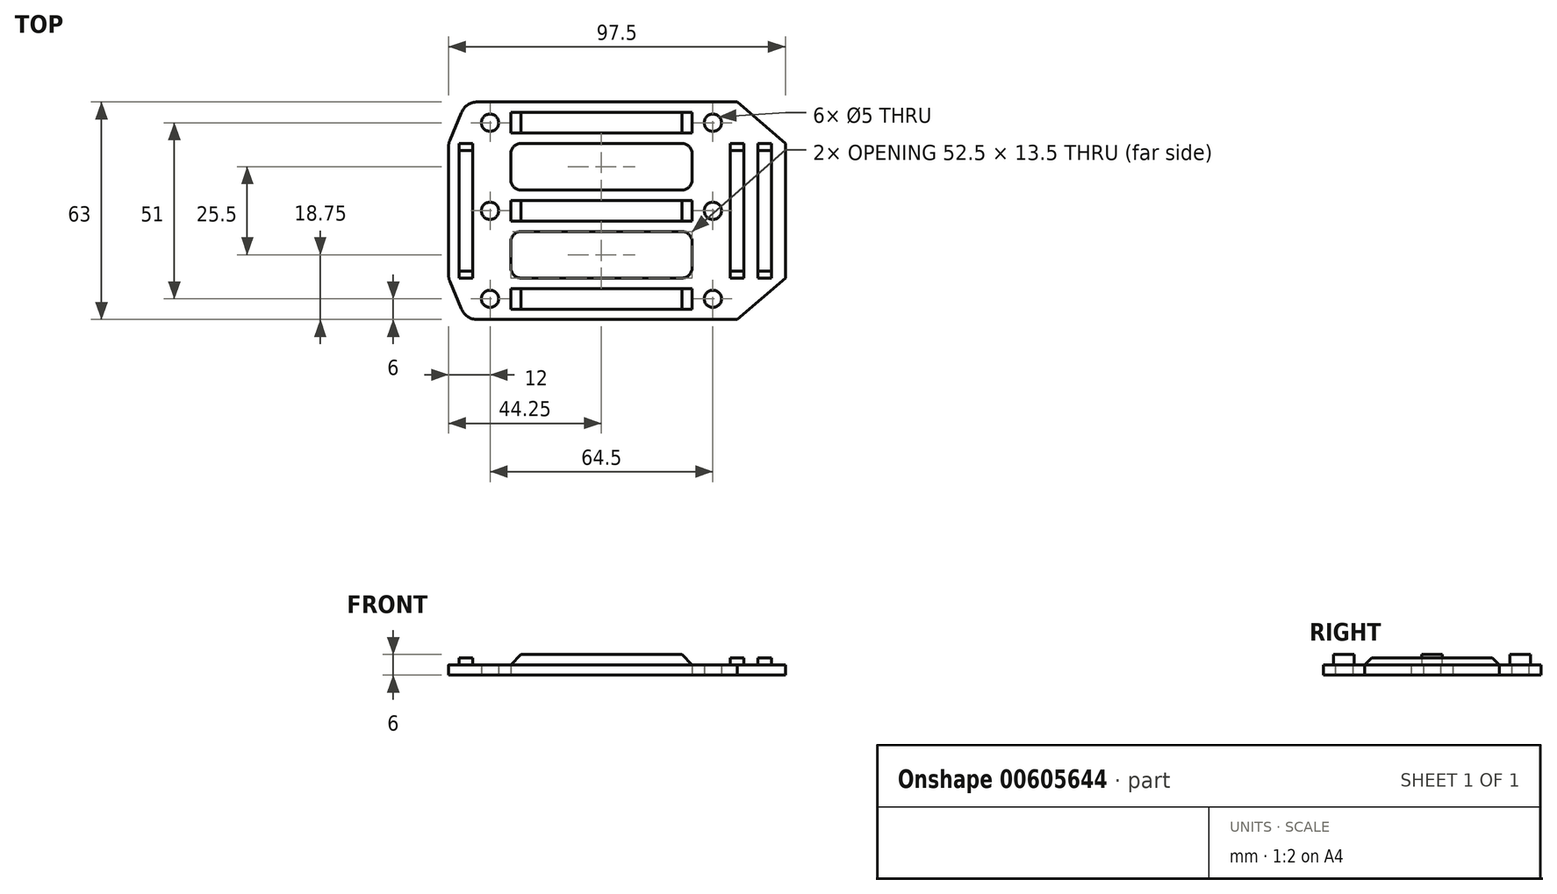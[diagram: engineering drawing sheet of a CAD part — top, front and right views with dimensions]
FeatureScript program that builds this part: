
annotation { "Feature Type Name" : "Feature", "Feature Type Description" : "" }
export const myFeature = defineFeature(function(context is Context, id is Id, definition is map)
    precondition{}
    {
        {
            var Q0;
            Q0=qCreatedBy(makeId("Top.planeOp"),FACE);
            var sketch = newSketch(context, id + "F0", { "sketchPlane" : qUnion([Q0])});
            skLineSegment(sketch, "E0.bottom", {"start": v(32.25, -25.5) * mm, "end": v(-32.25, -25.5) * mm});
            skLineSegment(sketch, "E0.top", {"start": v(32.25, 25.5) * mm, "end": v(-32.25, 25.5) * mm});
            skLineSegment(sketch, "E0.left", {"start": v(32.25, -25.5) * mm, "end": v(32.25, 25.5) * mm});
            skLineSegment(sketch, "E0.right", {"start": v(-32.25, -25.5) * mm, "end": v(-32.25, 25.5) * mm});
            skPoint(sketch, "E0.middle", {"position": v(0, 0) * mm});
            skLineSegment(sketch, "E1.0", {"start": v(-38.25, -28.5) * mm, "end": v(-38.25, 28.5) * mm});
            skLineSegment(sketch, "E1.1", {"start": v(35.25, -31.5) * mm, "end": v(-35.25, -31.5) * mm});
            skLineSegment(sketch, "E1.2", {"start": v(38.25, -28.5) * mm, "end": v(38.25, 28.5) * mm});
            skLineSegment(sketch, "E1.3", {"start": v(35.25, 31.5) * mm, "end": v(-35.25, 31.5) * mm});
            skCircle(sketch, "E2", {"center": v(-32.25, 25.5) * mm, "radius": 2.5 * mm});
            skCircle(sketch, "E3", {"center": v(-32.25, -25.5) * mm, "radius": 2.5 * mm});
            skCircle(sketch, "E4", {"center": v(32.25, 25.5) * mm, "radius": 2.5 * mm});
            skCircle(sketch, "E5", {"center": v(32.25, -25.5) * mm, "radius": 2.5 * mm});
            skCircle(sketch, "E6", {"center": v(-32.25, 0) * mm, "radius": 2.5 * mm});
            skCircle(sketch, "E7", {"center": v(32.25, 0) * mm, "radius": 2.5 * mm});
            skLineSegment(sketch, "E8.0", {"start": v(-26.25, -16.5) * mm, "end": v(-26.25, -9) * mm});
            skLineSegment(sketch, "E8.1", {"start": v(23.25, -19.5) * mm, "end": v(-23.25, -19.5) * mm});
            skLineSegment(sketch, "E8.2", {"start": v(26.25, -16.5) * mm, "end": v(26.25, -9) * mm});
            skLineSegment(sketch, "E8.3", {"start": v(23.25, 19.5) * mm, "end": v(-23.25, 19.5) * mm});
            skLineSegment(sketch, "E9", {"start": v(-32.25, 0) * mm, "end": v(32.25, 0) * mm, "construction": true});
            skLineSegment(sketch, "E10.0", {"start": v(-23.25, -6) * mm, "end": v(23.25, -6) * mm});
            skLineSegment(sketch, "E11.0", {"start": v(-23.25, 6) * mm, "end": v(23.25, 6) * mm});
            skPoint(sketch, "E12.visualSharp", {"position": v(-26.25, -19.5) * mm});
            skArc(sketch, "E12.filletArc", {"start": v(-26.25, -16.5) * mm, "mid": v(-25.37, -18.62) * mm, "end": v(-23.25, -19.5) * mm});
            skPoint(sketch, "E13.visualSharp", {"position": v(26.25, -19.5) * mm});
            skArc(sketch, "E13.filletArc", {"start": v(23.25, -19.5) * mm, "mid": v(25.37, -18.62) * mm, "end": v(26.25, -16.5) * mm});
            skPoint(sketch, "E14.visualSharp", {"position": v(26.25, 19.5) * mm});
            skArc(sketch, "E14.filletArc", {"start": v(26.25, 16.5) * mm, "mid": v(25.37, 18.62) * mm, "end": v(23.25, 19.5) * mm});
            skPoint(sketch, "E15.visualSharp", {"position": v(-26.25, 19.5) * mm});
            skArc(sketch, "E15.filletArc", {"start": v(-23.25, 19.5) * mm, "mid": v(-25.37, 18.62) * mm, "end": v(-26.25, 16.5) * mm});
            skPoint(sketch, "E16", {"position": v(-26.25, -6) * mm});
            skPoint(sketch, "E17", {"position": v(-26.25, 6) * mm});
            skLineSegment(sketch, "E18.trimOffspring", {"start": v(-26.25, 9) * mm, "end": v(-26.25, 16.5) * mm});
            skLineSegment(sketch, "E19.trimOffspring", {"start": v(26.25, 9) * mm, "end": v(26.25, 16.5) * mm});
            skArc(sketch, "E20.filletArc", {"start": v(-26.25, 9) * mm, "mid": v(-25.37, 6.88) * mm, "end": v(-23.25, 6) * mm});
            skArc(sketch, "E21.filletArc", {"start": v(23.25, 6) * mm, "mid": v(25.37, 6.88) * mm, "end": v(26.25, 9) * mm});
            skArc(sketch, "E22.filletArc", {"start": v(-23.25, -6) * mm, "mid": v(-25.37, -6.88) * mm, "end": v(-26.25, -9) * mm});
            skArc(sketch, "E23.filletArc", {"start": v(26.25, -9) * mm, "mid": v(25.37, -6.88) * mm, "end": v(23.25, -6) * mm});
            skPoint(sketch, "E24.visualSharp", {"position": v(-38.25, 31.5) * mm});
            skPoint(sketch, "E25.visualSharp", {"position": v(38.25, 31.5) * mm});
            skPoint(sketch, "E26.visualSharp", {"position": v(38.25, -31.5) * mm});
            skPoint(sketch, "E27.visualSharp", {"position": v(-38.25, -31.5) * mm});
            skLineSegment(sketch, "E28.bottom", {"start": v(26.25, -22.5) * mm, "end": v(-26.25, -22.5) * mm});
            skLineSegment(sketch, "E28.top", {"start": v(26.25, -28.5) * mm, "end": v(-26.25, -28.5) * mm});
            skLineSegment(sketch, "E28.left", {"start": v(26.25, -22.5) * mm, "end": v(26.25, -28.5) * mm});
            skLineSegment(sketch, "E28.right", {"start": v(-26.25, -22.5) * mm, "end": v(-26.25, -28.5) * mm});
            skPoint(sketch, "E28.middle", {"position": v(0, -25.5) * mm});
            skLineSegment(sketch, "E29.bottom", {"start": v(26.25, 22.5) * mm, "end": v(-26.25, 22.5) * mm});
            skLineSegment(sketch, "E29.top", {"start": v(26.25, 28.5) * mm, "end": v(-26.25, 28.5) * mm});
            skLineSegment(sketch, "E29.left", {"start": v(26.25, 22.5) * mm, "end": v(26.25, 28.5) * mm});
            skLineSegment(sketch, "E29.right", {"start": v(-26.25, 22.5) * mm, "end": v(-26.25, 28.5) * mm});
            skPoint(sketch, "E29.middle", {"position": v(0, 25.5) * mm});
            skLineSegment(sketch, "E30.bottom", {"start": v(26.25, 3) * mm, "end": v(-26.25, 3) * mm});
            skLineSegment(sketch, "E30.top", {"start": v(26.25, -3) * mm, "end": v(-26.25, -3) * mm});
            skLineSegment(sketch, "E30.left", {"start": v(26.25, 3) * mm, "end": v(26.25, -3) * mm});
            skLineSegment(sketch, "E30.right", {"start": v(-26.25, 3) * mm, "end": v(-26.25, -3) * mm});
            skLineSegment(sketch, "E31.bottom", {"start": v(38.25, -31.5) * mm, "end": v(41.25, -31.5) * mm});
            skLineSegment(sketch, "E31.top", {"start": v(38.25, 31.5) * mm, "end": v(41.25, 31.5) * mm});
            skLineSegment(sketch, "E31.left", {"start": v(38.25, -31.5) * mm, "end": v(38.25, 31.5) * mm});
            skLineSegment(sketch, "E31.right", {"start": v(44.25, -28.5) * mm, "end": v(44.25, 28.5) * mm});
            skLineSegment(sketch, "E32.bottom", {"start": v(-38.25, -31.5) * mm, "end": v(-41.25, -31.5) * mm});
            skLineSegment(sketch, "E32.top", {"start": v(-38.25, 31.5) * mm, "end": v(-41.25, 31.5) * mm});
            skLineSegment(sketch, "E32.left", {"start": v(-38.25, -31.5) * mm, "end": v(-38.25, 31.5) * mm});
            skLineSegment(sketch, "E32.right", {"start": v(-44.25, -28.5) * mm, "end": v(-44.25, 28.5) * mm});
            skLineSegment(sketch, "E33", {"start": v(-35.25, -31.5) * mm, "end": v(-38.25, -31.5) * mm});
            skLineSegment(sketch, "E34", {"start": v(35.25, -31.5) * mm, "end": v(38.25, -31.5) * mm});
            skLineSegment(sketch, "E35", {"start": v(35.25, 31.5) * mm, "end": v(38.25, 31.5) * mm});
            skLineSegment(sketch, "E36", {"start": v(-35.25, 31.5) * mm, "end": v(-38.25, 31.5) * mm});
            skPoint(sketch, "E37.visualSharp", {"position": v(-44.25, -31.5) * mm});
            skPoint(sketch, "E38.visualSharp", {"position": v(44.25, -31.5) * mm});
            skPoint(sketch, "E39.visualSharp", {"position": v(44.25, 31.5) * mm});
            skPoint(sketch, "E40.visualSharp", {"position": v(-44.25, 31.5) * mm});
            skLineSegment(sketch, "E41", {"start": v(41.25, 31.5) * mm, "end": v(44.25, 31.5) * mm});
            skLineSegment(sketch, "E42", {"start": v(44.25, 31.5) * mm, "end": v(44.25, 28.5) * mm});
            skLineSegment(sketch, "E43", {"start": v(-44.25, -28.5) * mm, "end": v(-44.25, -31.5) * mm});
            skLineSegment(sketch, "E44", {"start": v(-44.25, -31.5) * mm, "end": v(-41.25, -31.5) * mm});
            skLineSegment(sketch, "E45", {"start": v(-44.25, 28.5) * mm, "end": v(-44.25, 31.5) * mm});
            skLineSegment(sketch, "E46", {"start": v(-41.25, 31.5) * mm, "end": v(-44.25, 31.5) * mm});
            skLineSegment(sketch, "E47", {"start": v(41.25, -31.5) * mm, "end": v(44.25, -31.5) * mm});
            skLineSegment(sketch, "E48", {"start": v(44.25, -31.5) * mm, "end": v(44.25, -28.5) * mm});
            skSolve(sketch);
        }
        {
            var Q0;
            {var subQ5=sQuery(id+"F0.wireOp",EDGE,"E29.top");Q0=makeQuery(id+"F0.imprint","IMPRINT",FACE,{"disambiguationData":[TD([[makeQuery(id+"F0.imprint","IMPRINT",EDGE,{"derivedFrom":subQ5}),1.0]])]});}
            var Q1;
            {var subQ5=sQuery(id+"F0.wireOp",EDGE,"E29.bottom");Q1=makeQuery(id+"F0.imprint","IMPRINT",FACE,{"disambiguationData":[TD([[makeQuery(id+"F0.imprint","IMPRINT",EDGE,{"derivedFrom":subQ5}),-1.0]])]});}
            var Q2;
            Q2=makeQuery(id+"F0.imprint","IMPRINT",FACE,{"disambiguationData":[TD([[makeQuery(id+"F0.imprint","IMPRINT",EDGE,{"derivedFrom":sQuery(id+"F0.wireOp",EDGE,"E30.bottom")}),1.0]])]});
            var Q3;
            {var subQ5=sQuery(id+"F0.wireOp",EDGE,"E28.bottom");Q3=makeQuery(id+"F0.imprint","IMPRINT",FACE,{"disambiguationData":[TD([[makeQuery(id+"F0.imprint","IMPRINT",EDGE,{"derivedFrom":subQ5}),1.0]])]});}
            var Q4;
            {var subQ5=sQuery(id+"F0.wireOp",EDGE,"E28.top");Q4=makeQuery(id+"F0.imprint","IMPRINT",FACE,{"disambiguationData":[TD([[makeQuery(id+"F0.imprint","IMPRINT",EDGE,{"derivedFrom":subQ5}),-1.0]])]});}
            extrude(context, id + "F1", {"entities" : qUnion([Q0, Q1, Q2, Q3, Q4]), "depth" : 6 * mm, "offsetDistance" : 25 * mm});
        }
        {
            var Q0;
            Q0=makeQuery(id+"F0.imprint","IMPRINT",FACE,{"disambiguationData":[TD([[makeQuery(id+"F0.imprint","IMPRINT",EDGE,{"derivedFrom":sQuery(id+"F0.wireOp",EDGE,"E1.0")}),-1.0]])]});
            var Q1;
            Q1=makeQuery(id+"F0.imprint","IMPRINT",FACE,{"disambiguationData":[TD([[makeQuery(id+"F0.imprint","IMPRINT",EDGE,{"derivedFrom":sQuery(id+"F0.wireOp",EDGE,"E8.0")}),1.0]])]});
            var Q2;
            Q2=makeQuery(id+"F0.imprint","IMPRINT",FACE,{"disambiguationData":[TD([[makeQuery(id+"F0.imprint","IMPRINT",EDGE,{"derivedFrom":sQuery(id+"F0.wireOp",EDGE,"E1.1")}),-1.0]])]});
            var Q3;
            {var subQ3=sQuery(id+"F0.wireOp",EDGE,"E32.bottom");Q3=makeQuery(id+"F0.imprint","IMPRINT",FACE,{"disambiguationData":[TD([[makeQuery(id+"F0.imprint","IMPRINT",EDGE,{"derivedFrom":subQ3}),-1.0]])]});}
            var Q4;
            {var subQ3=sQuery(id+"F0.wireOp",EDGE,"E31.bottom");Q4=makeQuery(id+"F0.imprint","IMPRINT",FACE,{"disambiguationData":[TD([[makeQuery(id+"F0.imprint","IMPRINT",EDGE,{"derivedFrom":subQ3}),1.0]])]});}
            extrude(context, id + "F2", {"entities" : qUnion([Q0, Q1, Q2, Q3, Q4]), "depth" : 3 * mm, "offsetDistance" : 25 * mm});
        }
        {
            var Q0;
            Q0=makeQuery(id+"F1.opExtrude","SWEPT_BODY",BODY,{"disambiguationData":[OSD([sQuery(id+"F0.wireOp",EDGE,"E28.bottom"),sQuery(id+"F0.wireOp",EDGE,"E28.top"),sQuery(id+"F0.wireOp",EDGE,"E28.left"),sQuery(id+"F0.wireOp",EDGE,"E28.right")])]});
            var Q1;
            Q1=makeQuery(id+"F1.opExtrude","SWEPT_BODY",BODY,{"disambiguationData":[OSD([sQuery(id+"F0.wireOp",EDGE,"E29.bottom"),sQuery(id+"F0.wireOp",EDGE,"E29.top"),sQuery(id+"F0.wireOp",EDGE,"E29.left"),sQuery(id+"F0.wireOp",EDGE,"E29.right")])]});
            var Q2;
            Q2=makeQuery(id+"F1.opExtrude","SWEPT_BODY",BODY,{"disambiguationData":[OSD([sQuery(id+"F0.wireOp",EDGE,"E30.bottom"),sQuery(id+"F0.wireOp",EDGE,"E30.top"),sQuery(id+"F0.wireOp",EDGE,"E30.left"),sQuery(id+"F0.wireOp",EDGE,"E30.right")])]});
            var Q3;
            Q3=makeQuery(id+"F2.opExtrude","SWEPT_BODY",BODY,{"disambiguationData":[OSD([sQuery(id+"F0.wireOp",EDGE,"E1.0"),sQuery(id+"F0.wireOp",EDGE,"E1.1"),sQuery(id+"F0.wireOp",EDGE,"E1.2"),sQuery(id+"F0.wireOp",EDGE,"E1.3"),sQuery(id+"F0.wireOp",EDGE,"E2"),sQuery(id+"F0.wireOp",EDGE,"E3"),sQuery(id+"F0.wireOp",EDGE,"E4"),sQuery(id+"F0.wireOp",EDGE,"E5"),sQuery(id+"F0.wireOp",EDGE,"E6"),sQuery(id+"F0.wireOp",EDGE,"E7"),sQuery(id+"F0.wireOp",EDGE,"E8.0"),sQuery(id+"F0.wireOp",EDGE,"E8.1"),sQuery(id+"F0.wireOp",EDGE,"E8.2"),sQuery(id+"F0.wireOp",EDGE,"E8.3"),sQuery(id+"F0.wireOp",EDGE,"E10.0"),sQuery(id+"F0.wireOp",EDGE,"E11.0"),sQuery(id+"F0.wireOp",EDGE,"E12.filletArc"),sQuery(id+"F0.wireOp",EDGE,"E13.filletArc"),sQuery(id+"F0.wireOp",EDGE,"E14.filletArc"),sQuery(id+"F0.wireOp",EDGE,"E15.filletArc"),sQuery(id+"F0.wireOp",EDGE,"E18.trimOffspring"),sQuery(id+"F0.wireOp",EDGE,"E19.trimOffspring"),sQuery(id+"F0.wireOp",EDGE,"E20.filletArc"),sQuery(id+"F0.wireOp",EDGE,"E21.filletArc"),sQuery(id+"F0.wireOp",EDGE,"E22.filletArc"),sQuery(id+"F0.wireOp",EDGE,"E23.filletArc"),sQuery(id+"F0.wireOp",EDGE,"E24.filletArc"),sQuery(id+"F0.wireOp",EDGE,"E25.filletArc"),sQuery(id+"F0.wireOp",EDGE,"E26.filletArc"),sQuery(id+"F0.wireOp",EDGE,"E27.filletArc"),sQuery(id+"F0.wireOp",EDGE,"E28.bottom"),sQuery(id+"F0.wireOp",EDGE,"E28.top"),sQuery(id+"F0.wireOp",EDGE,"E28.left"),sQuery(id+"F0.wireOp",EDGE,"E28.right"),sQuery(id+"F0.wireOp",EDGE,"E29.bottom"),sQuery(id+"F0.wireOp",EDGE,"E29.top"),sQuery(id+"F0.wireOp",EDGE,"E29.left"),sQuery(id+"F0.wireOp",EDGE,"E29.right"),sQuery(id+"F0.wireOp",EDGE,"E30.bottom"),sQuery(id+"F0.wireOp",EDGE,"E30.top"),sQuery(id+"F0.wireOp",EDGE,"E30.left"),sQuery(id+"F0.wireOp",EDGE,"E30.right")])]});
            booleanBodies(context, id + "F3", {"operationType" : BooleanOperationType.UNION, "tools" : qUnion([Q0, Q1, Q2, Q3])});
        }
        {
            var Q0;
            Q0=makeQuery(id+"F1.opExtrude","CAP_EDGE",EDGE,{"disambiguationData":[OSD([sQuery(id+"F0.wireOp",EDGE,"E29.left")])],"isStart":false});
            var Q1;
            Q1=makeQuery(id+"F1.opExtrude","CAP_EDGE",EDGE,{"disambiguationData":[OSD([sQuery(id+"F0.wireOp",EDGE,"E30.left")])],"isStart":false});
            var Q2;
            Q2=makeQuery(id+"F1.opExtrude","CAP_EDGE",EDGE,{"disambiguationData":[OSD([sQuery(id+"F0.wireOp",EDGE,"E28.left")])],"isStart":false});
            var Q3;
            Q3=makeQuery(id+"F1.opExtrude","CAP_EDGE",EDGE,{"disambiguationData":[OSD([sQuery(id+"F0.wireOp",EDGE,"E29.right")])],"isStart":false});
            var Q4;
            Q4=makeQuery(id+"F1.opExtrude","CAP_EDGE",EDGE,{"disambiguationData":[OSD([sQuery(id+"F0.wireOp",EDGE,"E30.right")])],"isStart":false});
            var Q5;
            Q5=makeQuery(id+"F1.opExtrude","CAP_EDGE",EDGE,{"disambiguationData":[OSD([sQuery(id+"F0.wireOp",EDGE,"E28.right")])],"isStart":false});
            chamfer(context, id + "F4", {"entities" : qUnion([Q0, Q1, Q2, Q3, Q4, Q5]), "width" : 3 * mm, "tangentPropagation" : true});
        }
        {
            var Q0;
            Q0=makeQuery(id+"F2.opExtrude","SWEPT_EDGE",EDGE,{"disambiguationData":[OSD([sQuery(id+"F0.wireOp",EDGE,"E47"),sQuery(id+"F0.wireOp",EDGE,"E48")])]});
            var Q1;
            Q1=makeQuery(id+"F2.opExtrude","SWEPT_EDGE",EDGE,{"disambiguationData":[OSD([sQuery(id+"F0.wireOp",EDGE,"E41"),sQuery(id+"F0.wireOp",EDGE,"E42")])]});
            var Q2;
            Q2=makeQuery(id+"F2.opExtrude","SWEPT_EDGE",EDGE,{"disambiguationData":[OSD([sQuery(id+"F0.wireOp",EDGE,"E43"),sQuery(id+"F0.wireOp",EDGE,"E44")])]});
            var Q3;
            Q3=makeQuery(id+"F2.opExtrude","SWEPT_EDGE",EDGE,{"disambiguationData":[OSD([sQuery(id+"F0.wireOp",EDGE,"E45"),sQuery(id+"F0.wireOp",EDGE,"E46")])]});
            chamfer(context, id + "F5", {"entities" : qUnion([Q0, Q1, Q2, Q3]), "chamferType" : ChamferType.TWO_OFFSETS, "width1" : 12 * mm, "oppositeDirection" : false, "width2" : 6 * mm, "tangentPropagation" : true});
        }
        {
            var Q0;
            Q0=makeQuery(id+"F2.opExtrude","CAP_FACE",FACE,{"disambiguationData":[OSD([sQuery(id+"F0.wireOp",EDGE,"E1.1"),sQuery(id+"F0.wireOp",EDGE,"E1.3"),sQuery(id+"F0.wireOp",EDGE,"E2"),sQuery(id+"F0.wireOp",EDGE,"E3"),sQuery(id+"F0.wireOp",EDGE,"E4"),sQuery(id+"F0.wireOp",EDGE,"E5"),sQuery(id+"F0.wireOp",EDGE,"E6"),sQuery(id+"F0.wireOp",EDGE,"E7"),sQuery(id+"F0.wireOp",EDGE,"E8.0"),sQuery(id+"F0.wireOp",EDGE,"E8.1"),sQuery(id+"F0.wireOp",EDGE,"E8.2"),sQuery(id+"F0.wireOp",EDGE,"E8.3"),sQuery(id+"F0.wireOp",EDGE,"E10.0"),sQuery(id+"F0.wireOp",EDGE,"E11.0"),sQuery(id+"F0.wireOp",EDGE,"E12.filletArc"),sQuery(id+"F0.wireOp",EDGE,"E13.filletArc"),sQuery(id+"F0.wireOp",EDGE,"E14.filletArc"),sQuery(id+"F0.wireOp",EDGE,"E15.filletArc"),sQuery(id+"F0.wireOp",EDGE,"E18.trimOffspring"),sQuery(id+"F0.wireOp",EDGE,"E19.trimOffspring"),sQuery(id+"F0.wireOp",EDGE,"E20.filletArc"),sQuery(id+"F0.wireOp",EDGE,"E21.filletArc"),sQuery(id+"F0.wireOp",EDGE,"E22.filletArc"),sQuery(id+"F0.wireOp",EDGE,"E23.filletArc"),sQuery(id+"F0.wireOp",EDGE,"E28.bottom"),sQuery(id+"F0.wireOp",EDGE,"E28.top"),sQuery(id+"F0.wireOp",EDGE,"E28.left"),sQuery(id+"F0.wireOp",EDGE,"E28.right"),sQuery(id+"F0.wireOp",EDGE,"E29.bottom"),sQuery(id+"F0.wireOp",EDGE,"E29.top"),sQuery(id+"F0.wireOp",EDGE,"E29.left"),sQuery(id+"F0.wireOp",EDGE,"E29.right"),sQuery(id+"F0.wireOp",EDGE,"E30.bottom"),sQuery(id+"F0.wireOp",EDGE,"E30.top"),sQuery(id+"F0.wireOp",EDGE,"E30.left"),sQuery(id+"F0.wireOp",EDGE,"E30.right"),sQuery(id+"F0.wireOp",EDGE,"E31.bottom"),sQuery(id+"F0.wireOp",EDGE,"E31.top"),sQuery(id+"F0.wireOp",EDGE,"E31.right"),sQuery(id+"F0.wireOp",EDGE,"E32.bottom"),sQuery(id+"F0.wireOp",EDGE,"E32.top"),sQuery(id+"F0.wireOp",EDGE,"E32.right"),sQuery(id+"F0.wireOp",EDGE,"E33"),sQuery(id+"F0.wireOp",EDGE,"E34"),sQuery(id+"F0.wireOp",EDGE,"E35"),sQuery(id+"F0.wireOp",EDGE,"E36"),sQuery(id+"F0.wireOp",EDGE,"E41"),sQuery(id+"F0.wireOp",EDGE,"E42"),sQuery(id+"F0.wireOp",EDGE,"E43"),sQuery(id+"F0.wireOp",EDGE,"E44"),sQuery(id+"F0.wireOp",EDGE,"E45"),sQuery(id+"F0.wireOp",EDGE,"E46"),sQuery(id+"F0.wireOp",EDGE,"E47"),sQuery(id+"F0.wireOp",EDGE,"E48")])],"isStart":false});
            var sketch = newSketch(context, id + "F6", { "sketchPlane" : qUnion([Q0])});
            skLineSegment(sketch, "E49.0", {"start": v(-41.25, -19.5) * mm, "end": v(-41.25, 19.5) * mm});
            skLineSegment(sketch, "E50.0", {"start": v(41.25, -19.5) * mm, "end": v(41.25, 19.5) * mm});
            skLineSegment(sketch, "E51.bottom", {"start": v(-41.25, -19.5) * mm, "end": v(-37.25, -19.5) * mm});
            skLineSegment(sketch, "E51.top", {"start": v(-41.25, 19.5) * mm, "end": v(-37.25, 19.5) * mm});
            skLineSegment(sketch, "E51.right", {"start": v(-37.25, -19.5) * mm, "end": v(-37.25, 19.5) * mm});
            skLineSegment(sketch, "E52.bottom", {"start": v(41.25, -19.5) * mm, "end": v(37.25, -19.5) * mm});
            skLineSegment(sketch, "E52.top", {"start": v(41.25, 19.5) * mm, "end": v(37.25, 19.5) * mm});
            skLineSegment(sketch, "E52.right", {"start": v(37.25, -19.5) * mm, "end": v(37.25, 19.5) * mm});
            skSolve(sketch);
        }
        {
            var Q0;
            Q0=makeQuery(id+"F6.imprint","IMPRINT",FACE,{"disambiguationData":[TD([[makeQuery(id+"F6.imprint","IMPRINT",EDGE,{"derivedFrom":sQuery(id+"F6.wireOp",EDGE,"E51.bottom")}),1.0]])]});
            var Q1;
            Q1=makeQuery(id+"F6.imprint","IMPRINT",FACE,{"disambiguationData":[TD([[makeQuery(id+"F6.imprint","IMPRINT",EDGE,{"derivedFrom":sQuery(id+"F6.wireOp",EDGE,"E52.bottom")}),-1.0]])]});
            extrude(context, id + "F7", {"entities" : qUnion([Q0, Q1]), "operationType" : NewBodyOperationType.ADD, "depth" : 2 * mm, "offsetDistance" : 25 * mm});
        }
        {
            var Q0;
            Q0=makeQuery(id+"F7.opExtrude","CAP_EDGE",EDGE,{"disambiguationData":[OSD([sQuery(id+"F6.wireOp",EDGE,"E51.bottom")])],"isStart":false});
            var Q1;
            Q1=makeQuery(id+"F7.opExtrude","CAP_EDGE",EDGE,{"disambiguationData":[OSD([sQuery(id+"F6.wireOp",EDGE,"E51.top")])],"isStart":false});
            var Q2;
            Q2=makeQuery(id+"F7.opExtrude","CAP_EDGE",EDGE,{"disambiguationData":[OSD([sQuery(id+"F6.wireOp",EDGE,"E52.top")])],"isStart":false});
            var Q3;
            Q3=makeQuery(id+"F7.opExtrude","CAP_EDGE",EDGE,{"disambiguationData":[OSD([sQuery(id+"F6.wireOp",EDGE,"E52.bottom")])],"isStart":false});
            chamfer(context, id + "F8", {"entities" : qUnion([Q0, Q1, Q2, Q3]), "width" : 2 * mm, "tangentPropagation" : true});
        }
        {
            var Q0;
            {var subQ0=sQuery(id+"F0.wireOp",EDGE,"E30.right");var subQ1=sQuery(id+"F0.wireOp",EDGE,"E30.left");var subQ2=sQuery(id+"F0.wireOp",EDGE,"E30.top");var subQ3=sQuery(id+"F0.wireOp",EDGE,"E30.bottom");var subQ4=sQuery(id+"F0.wireOp",EDGE,"E29.right");var subQ5=sQuery(id+"F0.wireOp",EDGE,"E29.left");var subQ6=sQuery(id+"F0.wireOp",EDGE,"E29.top");var subQ7=sQuery(id+"F0.wireOp",EDGE,"E29.bottom");var subQ8=sQuery(id+"F0.wireOp",EDGE,"E28.right");var subQ9=sQuery(id+"F0.wireOp",EDGE,"E28.left");var subQ10=sQuery(id+"F0.wireOp",EDGE,"E28.top");var subQ11=sQuery(id+"F0.wireOp",EDGE,"E28.bottom");Q0=makeQuery(id+"F3.opBoolean","MERGE",FACE,{"derivedFrom":[makeQuery(id+"F1.opExtrude","CAP_FACE",FACE,{"disambiguationData":[OSD([subQ11,subQ10,subQ9,subQ8])],"isStart":true}),makeQuery(id+"F1.opExtrude","CAP_FACE",FACE,{"disambiguationData":[OSD([subQ7,subQ6,subQ5,subQ4])],"isStart":true}),makeQuery(id+"F1.opExtrude","CAP_FACE",FACE,{"disambiguationData":[OSD([subQ3,subQ2,subQ1,subQ0])],"isStart":true}),makeQuery(id+"F2.opExtrude","CAP_FACE",FACE,{"disambiguationData":[OSD([sQuery(id+"F0.wireOp",EDGE,"E1.1"),sQuery(id+"F0.wireOp",EDGE,"E1.3"),sQuery(id+"F0.wireOp",EDGE,"E2"),sQuery(id+"F0.wireOp",EDGE,"E3"),sQuery(id+"F0.wireOp",EDGE,"E4"),sQuery(id+"F0.wireOp",EDGE,"E5"),sQuery(id+"F0.wireOp",EDGE,"E6"),sQuery(id+"F0.wireOp",EDGE,"E7"),sQuery(id+"F0.wireOp",EDGE,"E8.0"),sQuery(id+"F0.wireOp",EDGE,"E8.1"),sQuery(id+"F0.wireOp",EDGE,"E8.2"),sQuery(id+"F0.wireOp",EDGE,"E8.3"),sQuery(id+"F0.wireOp",EDGE,"E10.0"),sQuery(id+"F0.wireOp",EDGE,"E11.0"),sQuery(id+"F0.wireOp",EDGE,"E12.filletArc"),sQuery(id+"F0.wireOp",EDGE,"E13.filletArc"),sQuery(id+"F0.wireOp",EDGE,"E14.filletArc"),sQuery(id+"F0.wireOp",EDGE,"E15.filletArc"),sQuery(id+"F0.wireOp",EDGE,"E18.trimOffspring"),sQuery(id+"F0.wireOp",EDGE,"E19.trimOffspring"),sQuery(id+"F0.wireOp",EDGE,"E20.filletArc"),sQuery(id+"F0.wireOp",EDGE,"E21.filletArc"),sQuery(id+"F0.wireOp",EDGE,"E22.filletArc"),sQuery(id+"F0.wireOp",EDGE,"E23.filletArc"),subQ11,subQ10,subQ9,subQ8,subQ7,subQ6,subQ5,subQ4,subQ3,subQ2,subQ1,subQ0,sQuery(id+"F0.wireOp",EDGE,"E31.bottom"),sQuery(id+"F0.wireOp",EDGE,"E31.top"),sQuery(id+"F0.wireOp",EDGE,"E31.right"),sQuery(id+"F0.wireOp",EDGE,"E32.bottom"),sQuery(id+"F0.wireOp",EDGE,"E32.top"),sQuery(id+"F0.wireOp",EDGE,"E32.right"),sQuery(id+"F0.wireOp",EDGE,"E33"),sQuery(id+"F0.wireOp",EDGE,"E34"),sQuery(id+"F0.wireOp",EDGE,"E35"),sQuery(id+"F0.wireOp",EDGE,"E36"),sQuery(id+"F0.wireOp",EDGE,"E41"),sQuery(id+"F0.wireOp",EDGE,"E42"),sQuery(id+"F0.wireOp",EDGE,"E43"),sQuery(id+"F0.wireOp",EDGE,"E44"),sQuery(id+"F0.wireOp",EDGE,"E45"),sQuery(id+"F0.wireOp",EDGE,"E46"),sQuery(id+"F0.wireOp",EDGE,"E47"),sQuery(id+"F0.wireOp",EDGE,"E48")])],"isStart":true})]});}
            var sketch = newSketch(context, id + "F9", { "sketchPlane" : qUnion([Q0])});
            skLineSegment(sketch, "E53", {"start": v(38.25, 31.5) * mm, "end": v(53.25, 31.5) * mm});
            skLineSegment(sketch, "E54", {"start": v(53.25, 31.5) * mm, "end": v(53.25, -31.5) * mm});
            skLineSegment(sketch, "E55", {"start": v(53.25, -31.5) * mm, "end": v(38.25, -31.5) * mm});
            skSolve(sketch);
        }
        {
            var Q0;
            Q0=makeQuery(id+"F9.imprint","IMPRINT",FACE,{"disambiguationData":[TD([[makeQuery(id+"F9.imprint","IMPRINT",EDGE,{"derivedFrom":sQuery(id+"F9.wireOp",EDGE,"E53")}),-1.0]])]});
            extrude(context, id + "F10", {"entities" : qUnion([Q0]), "oppositeDirection" : true, "depth" : 3 * mm, "offsetDistance" : 25 * mm});
        }
        {
            var Q0;
            Q0=makeQuery(id+"F1.opExtrude","SWEPT_BODY",BODY,{"disambiguationData":[OSD([sQuery(id+"F0.wireOp",EDGE,"E28.bottom"),sQuery(id+"F0.wireOp",EDGE,"E28.top"),sQuery(id+"F0.wireOp",EDGE,"E28.left"),sQuery(id+"F0.wireOp",EDGE,"E28.right")])]});
            var Q1;
            Q1=makeQuery(id+"F10.opExtrude","SWEPT_BODY",BODY,{"disambiguationData":[OSD([sQuery(id+"F0.wireOp",EDGE,"E1.1"),sQuery(id+"F0.wireOp",EDGE,"E1.3"),sQuery(id+"F0.wireOp",EDGE,"E2"),sQuery(id+"F0.wireOp",EDGE,"E3"),sQuery(id+"F0.wireOp",EDGE,"E4"),sQuery(id+"F0.wireOp",EDGE,"E5"),sQuery(id+"F0.wireOp",EDGE,"E6"),sQuery(id+"F0.wireOp",EDGE,"E7"),sQuery(id+"F0.wireOp",EDGE,"E8.0"),sQuery(id+"F0.wireOp",EDGE,"E8.1"),sQuery(id+"F0.wireOp",EDGE,"E8.2"),sQuery(id+"F0.wireOp",EDGE,"E8.3"),sQuery(id+"F0.wireOp",EDGE,"E10.0"),sQuery(id+"F0.wireOp",EDGE,"E11.0"),sQuery(id+"F0.wireOp",EDGE,"E12.filletArc"),sQuery(id+"F0.wireOp",EDGE,"E13.filletArc"),sQuery(id+"F0.wireOp",EDGE,"E14.filletArc"),sQuery(id+"F0.wireOp",EDGE,"E15.filletArc"),sQuery(id+"F0.wireOp",EDGE,"E18.trimOffspring"),sQuery(id+"F0.wireOp",EDGE,"E19.trimOffspring"),sQuery(id+"F0.wireOp",EDGE,"E20.filletArc"),sQuery(id+"F0.wireOp",EDGE,"E21.filletArc"),sQuery(id+"F0.wireOp",EDGE,"E22.filletArc"),sQuery(id+"F0.wireOp",EDGE,"E23.filletArc"),sQuery(id+"F0.wireOp",EDGE,"E28.bottom"),sQuery(id+"F0.wireOp",EDGE,"E28.top"),sQuery(id+"F0.wireOp",EDGE,"E28.left"),sQuery(id+"F0.wireOp",EDGE,"E28.right"),sQuery(id+"F0.wireOp",EDGE,"E29.bottom"),sQuery(id+"F0.wireOp",EDGE,"E29.top"),sQuery(id+"F0.wireOp",EDGE,"E29.left"),sQuery(id+"F0.wireOp",EDGE,"E29.right"),sQuery(id+"F0.wireOp",EDGE,"E30.bottom"),sQuery(id+"F0.wireOp",EDGE,"E30.top"),sQuery(id+"F0.wireOp",EDGE,"E30.left"),sQuery(id+"F0.wireOp",EDGE,"E30.right"),sQuery(id+"F0.wireOp",EDGE,"E31.bottom"),sQuery(id+"F0.wireOp",EDGE,"E31.top"),sQuery(id+"F0.wireOp",EDGE,"E31.right"),sQuery(id+"F0.wireOp",EDGE,"E32.bottom"),sQuery(id+"F0.wireOp",EDGE,"E32.top"),sQuery(id+"F0.wireOp",EDGE,"E32.right"),sQuery(id+"F0.wireOp",EDGE,"E33"),sQuery(id+"F0.wireOp",EDGE,"E34"),sQuery(id+"F0.wireOp",EDGE,"E35"),sQuery(id+"F0.wireOp",EDGE,"E36"),sQuery(id+"F0.wireOp",EDGE,"E41"),sQuery(id+"F0.wireOp",EDGE,"E42"),sQuery(id+"F0.wireOp",EDGE,"E43"),sQuery(id+"F0.wireOp",EDGE,"E44"),sQuery(id+"F0.wireOp",EDGE,"E45"),sQuery(id+"F0.wireOp",EDGE,"E46"),sQuery(id+"F0.wireOp",EDGE,"E47"),sQuery(id+"F0.wireOp",EDGE,"E48"),sQuery(id+"F9.wireOp",EDGE,"E53"),sQuery(id+"F9.wireOp",EDGE,"E54"),sQuery(id+"F9.wireOp",EDGE,"E55")])]});
            booleanBodies(context, id + "F11", {"operationType" : BooleanOperationType.UNION, "tools" : qUnion([Q0, Q1])});
        }
        {
            var Q0;
            {var subQ0=sQuery(id+"F0.wireOp",EDGE,"E48");var subQ1=sQuery(id+"F0.wireOp",EDGE,"E47");var subQ2=sQuery(id+"F0.wireOp",EDGE,"E46");var subQ3=sQuery(id+"F0.wireOp",EDGE,"E45");var subQ4=sQuery(id+"F0.wireOp",EDGE,"E44");var subQ5=sQuery(id+"F0.wireOp",EDGE,"E43");var subQ6=sQuery(id+"F0.wireOp",EDGE,"E42");var subQ7=sQuery(id+"F0.wireOp",EDGE,"E41");var subQ8=sQuery(id+"F0.wireOp",EDGE,"E36");var subQ9=sQuery(id+"F0.wireOp",EDGE,"E35");var subQ10=sQuery(id+"F0.wireOp",EDGE,"E34");var subQ11=sQuery(id+"F0.wireOp",EDGE,"E33");var subQ12=sQuery(id+"F0.wireOp",EDGE,"E32.right");var subQ13=sQuery(id+"F0.wireOp",EDGE,"E32.top");var subQ14=sQuery(id+"F0.wireOp",EDGE,"E32.bottom");var subQ15=sQuery(id+"F0.wireOp",EDGE,"E31.right");var subQ16=sQuery(id+"F0.wireOp",EDGE,"E31.top");var subQ17=sQuery(id+"F0.wireOp",EDGE,"E31.bottom");var subQ18=sQuery(id+"F0.wireOp",EDGE,"E30.right");var subQ19=sQuery(id+"F0.wireOp",EDGE,"E30.left");var subQ20=sQuery(id+"F0.wireOp",EDGE,"E30.top");var subQ21=sQuery(id+"F0.wireOp",EDGE,"E30.bottom");var subQ22=sQuery(id+"F0.wireOp",EDGE,"E29.right");var subQ23=sQuery(id+"F0.wireOp",EDGE,"E29.left");var subQ24=sQuery(id+"F0.wireOp",EDGE,"E29.top");var subQ25=sQuery(id+"F0.wireOp",EDGE,"E29.bottom");var subQ26=sQuery(id+"F0.wireOp",EDGE,"E28.right");var subQ27=sQuery(id+"F0.wireOp",EDGE,"E28.left");var subQ28=sQuery(id+"F0.wireOp",EDGE,"E28.top");var subQ29=sQuery(id+"F0.wireOp",EDGE,"E28.bottom");var subQ30=sQuery(id+"F0.wireOp",EDGE,"E23.filletArc");var subQ31=sQuery(id+"F0.wireOp",EDGE,"E22.filletArc");var subQ32=sQuery(id+"F0.wireOp",EDGE,"E21.filletArc");var subQ33=sQuery(id+"F0.wireOp",EDGE,"E20.filletArc");var subQ34=sQuery(id+"F0.wireOp",EDGE,"E19.trimOffspring");var subQ35=sQuery(id+"F0.wireOp",EDGE,"E18.trimOffspring");var subQ36=sQuery(id+"F0.wireOp",EDGE,"E15.filletArc");var subQ37=sQuery(id+"F0.wireOp",EDGE,"E14.filletArc");var subQ38=sQuery(id+"F0.wireOp",EDGE,"E13.filletArc");var subQ39=sQuery(id+"F0.wireOp",EDGE,"E12.filletArc");var subQ40=sQuery(id+"F0.wireOp",EDGE,"E11.0");var subQ41=sQuery(id+"F0.wireOp",EDGE,"E10.0");var subQ42=sQuery(id+"F0.wireOp",EDGE,"E8.3");var subQ43=sQuery(id+"F0.wireOp",EDGE,"E8.2");var subQ44=sQuery(id+"F0.wireOp",EDGE,"E8.1");var subQ45=sQuery(id+"F0.wireOp",EDGE,"E8.0");var subQ46=sQuery(id+"F0.wireOp",EDGE,"E7");var subQ47=sQuery(id+"F0.wireOp",EDGE,"E6");var subQ48=sQuery(id+"F0.wireOp",EDGE,"E5");var subQ49=sQuery(id+"F0.wireOp",EDGE,"E4");var subQ50=sQuery(id+"F0.wireOp",EDGE,"E3");var subQ51=sQuery(id+"F0.wireOp",EDGE,"E2");var subQ52=sQuery(id+"F0.wireOp",EDGE,"E1.3");var subQ53=sQuery(id+"F0.wireOp",EDGE,"E1.1");Q0=makeQuery(id+"F11.opBoolean","MERGE",FACE,{"derivedFrom":[makeQuery(id+"F2.opExtrude","CAP_FACE",FACE,{"disambiguationData":[OSD([subQ53,subQ52,subQ51,subQ50,subQ49,subQ48,subQ47,subQ46,subQ45,subQ44,subQ43,subQ42,subQ41,subQ40,subQ39,subQ38,subQ37,subQ36,subQ35,subQ34,subQ33,subQ32,subQ31,subQ30,subQ29,subQ28,subQ27,subQ26,subQ25,subQ24,subQ23,subQ22,subQ21,subQ20,subQ19,subQ18,subQ17,subQ16,subQ15,subQ14,subQ13,subQ12,subQ11,subQ10,subQ9,subQ8,subQ7,subQ6,subQ5,subQ4,subQ3,subQ2,subQ1,subQ0])],"isStart":false}),makeQuery(id+"F10.opExtrude","CAP_FACE",FACE,{"disambiguationData":[OSD([subQ53,subQ52,subQ51,subQ50,subQ49,subQ48,subQ47,subQ46,subQ45,subQ44,subQ43,subQ42,subQ41,subQ40,subQ39,subQ38,subQ37,subQ36,subQ35,subQ34,subQ33,subQ32,subQ31,subQ30,subQ29,subQ28,subQ27,subQ26,subQ25,subQ24,subQ23,subQ22,subQ21,subQ20,subQ19,subQ18,subQ17,subQ16,subQ15,subQ14,subQ13,subQ12,subQ11,subQ10,subQ9,subQ8,subQ7,subQ6,subQ5,subQ4,subQ3,subQ2,subQ1,subQ0,sQuery(id+"F9.wireOp",EDGE,"E53"),sQuery(id+"F9.wireOp",EDGE,"E54"),sQuery(id+"F9.wireOp",EDGE,"E55")])],"isStart":false})]});}
            var sketch = newSketch(context, id + "F12", { "sketchPlane" : qUnion([Q0])});
            skPoint(sketch, "E56", {"position": v(53.25, 19.5) * mm});
            skPoint(sketch, "E57", {"position": v(53.25, -19.5) * mm});
            skPoint(sketch, "E58", {"position": v(39.25, -31.5) * mm});
            skPoint(sketch, "E58.positionSnap0", {"position": v(39.25, -19.5) * mm});
            skPoint(sketch, "E59", {"position": v(39.25, 31.5) * mm});
            skPoint(sketch, "E59.positionSnap0", {"position": v(39.25, 19.5) * mm});
            skPoint(sketch, "E60", {"position": v(-39.25, -31.5) * mm});
            skPoint(sketch, "E60.positionSnap0", {"position": v(-39.25, -19.5) * mm});
            skPoint(sketch, "E61", {"position": v(-39.25, 31.5) * mm});
            skPoint(sketch, "E61.positionSnap0", {"position": v(-39.25, 19.5) * mm});
            skLineSegment(sketch, "E62", {"start": v(-39.25, 31.5) * mm, "end": v(-44.25, 19.5) * mm});
            skLineSegment(sketch, "E63", {"start": v(-39.25, -31.5) * mm, "end": v(-44.25, -19.5) * mm});
            skLineSegment(sketch, "E64", {"start": v(-39.25, 31.5) * mm, "end": v(-38.25, 31.5) * mm});
            skLineSegment(sketch, "E65", {"start": v(-39.25, -31.5) * mm, "end": v(-38.25, -31.5) * mm});
            skPoint(sketch, "E66", {"position": v(45.25, -19.5) * mm});
            skLineSegment(sketch, "E67.bottom", {"start": v(45.25, -19.5) * mm, "end": v(49.25, -19.5) * mm});
            skLineSegment(sketch, "E67.top", {"start": v(45.25, 19.5) * mm, "end": v(49.25, 19.5) * mm});
            skLineSegment(sketch, "E67.left", {"start": v(45.25, -19.5) * mm, "end": v(45.25, 19.5) * mm});
            skLineSegment(sketch, "E67.right", {"start": v(49.25, -19.5) * mm, "end": v(49.25, 19.5) * mm});
            skLineSegment(sketch, "E68", {"start": v(39.25, -31.5) * mm, "end": v(53.25, -19.5) * mm});
            skLineSegment(sketch, "E69", {"start": v(53.25, 19.5) * mm, "end": v(39.25, 31.5) * mm});
            skSolve(sketch);
        }
        {
            var Q0;
            Q0=makeQuery(id+"F12.imprint","IMPRINT",FACE,{"disambiguationData":[TD([[makeQuery(id+"F12.imprint","IMPRINT",EDGE,{"derivedFrom":sQuery(id+"F12.wireOp",EDGE,"E63")}),-1.0]])]});
            var Q1;
            Q1=makeQuery(id+"F12.imprint","IMPRINT",FACE,{"disambiguationData":[TD([[makeQuery(id+"F12.imprint","IMPRINT",EDGE,{"derivedFrom":sQuery(id+"F12.wireOp",EDGE,"E62")}),1.0]])]});
            extrude(context, id + "F13", {"entities" : qUnion([Q0, Q1]), "oppositeDirection" : true, "depth" : 3 * mm, "offsetDistance" : 25 * mm});
        }
        {
            var Q0;
            Q0=makeQuery(id+"F1.opExtrude","SWEPT_BODY",BODY,{"disambiguationData":[OSD([sQuery(id+"F0.wireOp",EDGE,"E28.bottom"),sQuery(id+"F0.wireOp",EDGE,"E28.top"),sQuery(id+"F0.wireOp",EDGE,"E28.left"),sQuery(id+"F0.wireOp",EDGE,"E28.right")])]});
            var Q1;
            Q1=makeQuery(id+"F13.opExtrude","SWEPT_BODY",BODY,{"disambiguationData":[OSD([sQuery(id+"F0.wireOp",EDGE,"E1.1"),sQuery(id+"F0.wireOp",EDGE,"E1.3"),sQuery(id+"F0.wireOp",EDGE,"E2"),sQuery(id+"F0.wireOp",EDGE,"E3"),sQuery(id+"F0.wireOp",EDGE,"E4"),sQuery(id+"F0.wireOp",EDGE,"E5"),sQuery(id+"F0.wireOp",EDGE,"E6"),sQuery(id+"F0.wireOp",EDGE,"E7"),sQuery(id+"F0.wireOp",EDGE,"E8.0"),sQuery(id+"F0.wireOp",EDGE,"E8.1"),sQuery(id+"F0.wireOp",EDGE,"E8.2"),sQuery(id+"F0.wireOp",EDGE,"E8.3"),sQuery(id+"F0.wireOp",EDGE,"E10.0"),sQuery(id+"F0.wireOp",EDGE,"E11.0"),sQuery(id+"F0.wireOp",EDGE,"E12.filletArc"),sQuery(id+"F0.wireOp",EDGE,"E13.filletArc"),sQuery(id+"F0.wireOp",EDGE,"E14.filletArc"),sQuery(id+"F0.wireOp",EDGE,"E15.filletArc"),sQuery(id+"F0.wireOp",EDGE,"E18.trimOffspring"),sQuery(id+"F0.wireOp",EDGE,"E19.trimOffspring"),sQuery(id+"F0.wireOp",EDGE,"E20.filletArc"),sQuery(id+"F0.wireOp",EDGE,"E21.filletArc"),sQuery(id+"F0.wireOp",EDGE,"E22.filletArc"),sQuery(id+"F0.wireOp",EDGE,"E23.filletArc"),sQuery(id+"F0.wireOp",EDGE,"E28.bottom"),sQuery(id+"F0.wireOp",EDGE,"E28.top"),sQuery(id+"F0.wireOp",EDGE,"E28.left"),sQuery(id+"F0.wireOp",EDGE,"E28.right"),sQuery(id+"F0.wireOp",EDGE,"E29.bottom"),sQuery(id+"F0.wireOp",EDGE,"E29.top"),sQuery(id+"F0.wireOp",EDGE,"E29.left"),sQuery(id+"F0.wireOp",EDGE,"E29.right"),sQuery(id+"F0.wireOp",EDGE,"E30.bottom"),sQuery(id+"F0.wireOp",EDGE,"E30.top"),sQuery(id+"F0.wireOp",EDGE,"E30.left"),sQuery(id+"F0.wireOp",EDGE,"E30.right"),sQuery(id+"F0.wireOp",EDGE,"E31.bottom"),sQuery(id+"F0.wireOp",EDGE,"E31.top"),sQuery(id+"F0.wireOp",EDGE,"E31.right"),sQuery(id+"F0.wireOp",EDGE,"E32.bottom"),sQuery(id+"F0.wireOp",EDGE,"E32.top"),sQuery(id+"F0.wireOp",EDGE,"E32.right"),sQuery(id+"F0.wireOp",EDGE,"E33"),sQuery(id+"F0.wireOp",EDGE,"E34"),sQuery(id+"F0.wireOp",EDGE,"E35"),sQuery(id+"F0.wireOp",EDGE,"E36"),sQuery(id+"F0.wireOp",EDGE,"E41"),sQuery(id+"F0.wireOp",EDGE,"E42"),sQuery(id+"F0.wireOp",EDGE,"E43"),sQuery(id+"F0.wireOp",EDGE,"E44"),sQuery(id+"F0.wireOp",EDGE,"E45"),sQuery(id+"F0.wireOp",EDGE,"E46"),sQuery(id+"F0.wireOp",EDGE,"E47"),sQuery(id+"F0.wireOp",EDGE,"E48"),sQuery(id+"F12.wireOp",EDGE,"E62"),sQuery(id+"F12.wireOp",EDGE,"E64")])]});
            var Q2;
            Q2=makeQuery(id+"F13.opExtrude","SWEPT_BODY",BODY,{"disambiguationData":[OSD([sQuery(id+"F0.wireOp",EDGE,"E1.1"),sQuery(id+"F0.wireOp",EDGE,"E1.3"),sQuery(id+"F0.wireOp",EDGE,"E2"),sQuery(id+"F0.wireOp",EDGE,"E3"),sQuery(id+"F0.wireOp",EDGE,"E4"),sQuery(id+"F0.wireOp",EDGE,"E5"),sQuery(id+"F0.wireOp",EDGE,"E6"),sQuery(id+"F0.wireOp",EDGE,"E7"),sQuery(id+"F0.wireOp",EDGE,"E8.0"),sQuery(id+"F0.wireOp",EDGE,"E8.1"),sQuery(id+"F0.wireOp",EDGE,"E8.2"),sQuery(id+"F0.wireOp",EDGE,"E8.3"),sQuery(id+"F0.wireOp",EDGE,"E10.0"),sQuery(id+"F0.wireOp",EDGE,"E11.0"),sQuery(id+"F0.wireOp",EDGE,"E12.filletArc"),sQuery(id+"F0.wireOp",EDGE,"E13.filletArc"),sQuery(id+"F0.wireOp",EDGE,"E14.filletArc"),sQuery(id+"F0.wireOp",EDGE,"E15.filletArc"),sQuery(id+"F0.wireOp",EDGE,"E18.trimOffspring"),sQuery(id+"F0.wireOp",EDGE,"E19.trimOffspring"),sQuery(id+"F0.wireOp",EDGE,"E20.filletArc"),sQuery(id+"F0.wireOp",EDGE,"E21.filletArc"),sQuery(id+"F0.wireOp",EDGE,"E22.filletArc"),sQuery(id+"F0.wireOp",EDGE,"E23.filletArc"),sQuery(id+"F0.wireOp",EDGE,"E28.bottom"),sQuery(id+"F0.wireOp",EDGE,"E28.top"),sQuery(id+"F0.wireOp",EDGE,"E28.left"),sQuery(id+"F0.wireOp",EDGE,"E28.right"),sQuery(id+"F0.wireOp",EDGE,"E29.bottom"),sQuery(id+"F0.wireOp",EDGE,"E29.top"),sQuery(id+"F0.wireOp",EDGE,"E29.left"),sQuery(id+"F0.wireOp",EDGE,"E29.right"),sQuery(id+"F0.wireOp",EDGE,"E30.bottom"),sQuery(id+"F0.wireOp",EDGE,"E30.top"),sQuery(id+"F0.wireOp",EDGE,"E30.left"),sQuery(id+"F0.wireOp",EDGE,"E30.right"),sQuery(id+"F0.wireOp",EDGE,"E31.bottom"),sQuery(id+"F0.wireOp",EDGE,"E31.top"),sQuery(id+"F0.wireOp",EDGE,"E31.right"),sQuery(id+"F0.wireOp",EDGE,"E32.bottom"),sQuery(id+"F0.wireOp",EDGE,"E32.top"),sQuery(id+"F0.wireOp",EDGE,"E32.right"),sQuery(id+"F0.wireOp",EDGE,"E33"),sQuery(id+"F0.wireOp",EDGE,"E34"),sQuery(id+"F0.wireOp",EDGE,"E35"),sQuery(id+"F0.wireOp",EDGE,"E36"),sQuery(id+"F0.wireOp",EDGE,"E41"),sQuery(id+"F0.wireOp",EDGE,"E42"),sQuery(id+"F0.wireOp",EDGE,"E43"),sQuery(id+"F0.wireOp",EDGE,"E44"),sQuery(id+"F0.wireOp",EDGE,"E45"),sQuery(id+"F0.wireOp",EDGE,"E46"),sQuery(id+"F0.wireOp",EDGE,"E47"),sQuery(id+"F0.wireOp",EDGE,"E48"),sQuery(id+"F12.wireOp",EDGE,"E63"),sQuery(id+"F12.wireOp",EDGE,"E65")])]});
            booleanBodies(context, id + "F14", {"operationType" : BooleanOperationType.UNION, "tools" : qUnion([Q0, Q1, Q2])});
        }
        {
            var Q0;
            Q0=makeQuery(id+"F12.imprint","IMPRINT",FACE,{"disambiguationData":[TD([[makeQuery(id+"F12.imprint","IMPRINT",EDGE,{"derivedFrom":sQuery(id+"F12.wireOp",EDGE,"E67.bottom")}),1.0]])]});
            extrude(context, id + "F15", {"entities" : qUnion([Q0]), "operationType" : NewBodyOperationType.ADD, "depth" : 2 * mm, "offsetDistance" : 25 * mm});
        }
        {
            var Q0;
            Q0=makeQuery(id+"F15.opExtrude","CAP_EDGE",EDGE,{"disambiguationData":[OSD([sQuery(id+"F12.wireOp",EDGE,"E67.bottom")])],"isStart":false});
            chamfer(context, id + "F16", {"entities" : qUnion([Q0]), "width" : 2 * mm, "tangentPropagation" : true});
        }
        {
            var Q0;
            Q0=makeQuery(id+"F15.opExtrude","CAP_EDGE",EDGE,{"disambiguationData":[OSD([sQuery(id+"F12.wireOp",EDGE,"E67.top")])],"isStart":false});
            chamfer(context, id + "F17", {"entities" : qUnion([Q0]), "width" : 2 * mm, "tangentPropagation" : true});
        }
        {
            var Q0;
            {var subQ0=sQuery(id+"F12.wireOp",EDGE,"E69");Q0=makeQuery(id+"F12.imprint","IMPRINT",FACE,{"disambiguationData":[TD([[makeQuery(id+"F12.imprint","IMPRINT",EDGE,{"derivedFrom":subQ0}),-1.0]])]});}
            var Q1;
            {var subQ0=sQuery(id+"F12.wireOp",EDGE,"E68");Q1=makeQuery(id+"F12.imprint","IMPRINT",FACE,{"disambiguationData":[TD([[makeQuery(id+"F12.imprint","IMPRINT",EDGE,{"derivedFrom":subQ0}),-1.0]])]});}
            extrude(context, id + "F18", {"entities" : qUnion([Q0, Q1]), "operationType" : NewBodyOperationType.REMOVE, "oppositeDirection" : true, "depth" : 25 * mm, "offsetDistance" : 25 * mm});
        }
        {
            var Q0;
            Q0=makeQuery(id+"F18.boolean.opBoolean","COPY",EDGE,{"derivedFrom":makeQuery(id+"F18.opExtrude","SWEPT_EDGE",EDGE,{"disambiguationData":[OSD([sQuery(id+"F0.wireOp",EDGE,"E1.1"),sQuery(id+"F0.wireOp",EDGE,"E31.bottom"),sQuery(id+"F0.wireOp",EDGE,"E32.bottom"),sQuery(id+"F0.wireOp",EDGE,"E33"),sQuery(id+"F0.wireOp",EDGE,"E34"),sQuery(id+"F0.wireOp",EDGE,"E44"),sQuery(id+"F0.wireOp",EDGE,"E47"),sQuery(id+"F9.wireOp",EDGE,"E53"),sQuery(id+"F12.wireOp",EDGE,"E68")])]})});
            var Q1;
            Q1=makeQuery(id+"F18.boolean.opBoolean","COPY",EDGE,{"derivedFrom":makeQuery(id+"F18.opExtrude","SWEPT_EDGE",EDGE,{"disambiguationData":[OSD([sQuery(id+"F9.wireOp",EDGE,"E54"),sQuery(id+"F12.wireOp",EDGE,"E68")])]})});
            var Q2;
            Q2=makeQuery(id+"F13.opExtrude","SWEPT_EDGE",EDGE,{"disambiguationData":[OSD([sQuery(id+"F12.wireOp",EDGE,"E63"),sQuery(id+"F12.wireOp",EDGE,"E65")])]});
            var Q3;
            {var subQ0=sQuery(id+"F0.wireOp",EDGE,"E45");var subQ1=sQuery(id+"F0.wireOp",EDGE,"E44");var subQ2=sQuery(id+"F0.wireOp",EDGE,"E43");var subQ3=sQuery(id+"F0.wireOp",EDGE,"E32.right");Q3=makeQuery(id+"F14.opBoolean","MERGE",EDGE,{"derivedFrom":[makeQuery(id+"F5.opChamfer","BLEND_EDGE",EDGE,{"blendedFrom":[makeQuery(id+"F2.opExtrude","SWEPT_EDGE",EDGE,{"disambiguationData":[OSD([subQ2,subQ1])]}),makeQuery(id+"F2.opExtrude","SWEPT_FACE",FACE,{"disambiguationData":[OSD([subQ3,subQ2,subQ0])]})],"blendedInto":[makeQuery(id+"F2.opExtrude","SWEPT_FACE",FACE,{"disambiguationData":[OSD([subQ3,subQ2,subQ0])]})]}),makeQuery(id+"F13.opExtrude","SWEPT_EDGE",EDGE,{"disambiguationData":[OSD([sQuery(id+"F0.wireOp",EDGE,"E1.1"),sQuery(id+"F0.wireOp",EDGE,"E1.3"),sQuery(id+"F0.wireOp",EDGE,"E2"),sQuery(id+"F0.wireOp",EDGE,"E3"),sQuery(id+"F0.wireOp",EDGE,"E4"),sQuery(id+"F0.wireOp",EDGE,"E5"),sQuery(id+"F0.wireOp",EDGE,"E6"),sQuery(id+"F0.wireOp",EDGE,"E7"),sQuery(id+"F0.wireOp",EDGE,"E8.0"),sQuery(id+"F0.wireOp",EDGE,"E8.1"),sQuery(id+"F0.wireOp",EDGE,"E8.2"),sQuery(id+"F0.wireOp",EDGE,"E8.3"),sQuery(id+"F0.wireOp",EDGE,"E10.0"),sQuery(id+"F0.wireOp",EDGE,"E11.0"),sQuery(id+"F0.wireOp",EDGE,"E12.filletArc"),sQuery(id+"F0.wireOp",EDGE,"E13.filletArc"),sQuery(id+"F0.wireOp",EDGE,"E14.filletArc"),sQuery(id+"F0.wireOp",EDGE,"E15.filletArc"),sQuery(id+"F0.wireOp",EDGE,"E18.trimOffspring"),sQuery(id+"F0.wireOp",EDGE,"E19.trimOffspring"),sQuery(id+"F0.wireOp",EDGE,"E20.filletArc"),sQuery(id+"F0.wireOp",EDGE,"E21.filletArc"),sQuery(id+"F0.wireOp",EDGE,"E22.filletArc"),sQuery(id+"F0.wireOp",EDGE,"E23.filletArc"),sQuery(id+"F0.wireOp",EDGE,"E28.bottom"),sQuery(id+"F0.wireOp",EDGE,"E28.top"),sQuery(id+"F0.wireOp",EDGE,"E28.left"),sQuery(id+"F0.wireOp",EDGE,"E28.right"),sQuery(id+"F0.wireOp",EDGE,"E29.bottom"),sQuery(id+"F0.wireOp",EDGE,"E29.top"),sQuery(id+"F0.wireOp",EDGE,"E29.left"),sQuery(id+"F0.wireOp",EDGE,"E29.right"),sQuery(id+"F0.wireOp",EDGE,"E30.bottom"),sQuery(id+"F0.wireOp",EDGE,"E30.top"),sQuery(id+"F0.wireOp",EDGE,"E30.left"),sQuery(id+"F0.wireOp",EDGE,"E30.right"),sQuery(id+"F0.wireOp",EDGE,"E31.bottom"),sQuery(id+"F0.wireOp",EDGE,"E31.top"),sQuery(id+"F0.wireOp",EDGE,"E31.right"),sQuery(id+"F0.wireOp",EDGE,"E32.bottom"),sQuery(id+"F0.wireOp",EDGE,"E32.top"),subQ3,sQuery(id+"F0.wireOp",EDGE,"E33"),sQuery(id+"F0.wireOp",EDGE,"E34"),sQuery(id+"F0.wireOp",EDGE,"E35"),sQuery(id+"F0.wireOp",EDGE,"E36"),sQuery(id+"F0.wireOp",EDGE,"E41"),sQuery(id+"F0.wireOp",EDGE,"E42"),subQ2,subQ1,subQ0,sQuery(id+"F0.wireOp",EDGE,"E46"),sQuery(id+"F0.wireOp",EDGE,"E47"),sQuery(id+"F0.wireOp",EDGE,"E48"),sQuery(id+"F12.wireOp",EDGE,"E63")])]})]});}
            var Q4;
            {var subQ0=sQuery(id+"F0.wireOp",EDGE,"E46");var subQ1=sQuery(id+"F0.wireOp",EDGE,"E45");var subQ2=sQuery(id+"F0.wireOp",EDGE,"E43");var subQ3=sQuery(id+"F0.wireOp",EDGE,"E32.right");Q4=makeQuery(id+"F14.opBoolean","MERGE",EDGE,{"derivedFrom":[makeQuery(id+"F5.opChamfer","BLEND_EDGE",EDGE,{"blendedFrom":[makeQuery(id+"F2.opExtrude","SWEPT_EDGE",EDGE,{"disambiguationData":[OSD([subQ1,subQ0])]}),makeQuery(id+"F2.opExtrude","SWEPT_FACE",FACE,{"disambiguationData":[OSD([subQ3,subQ2,subQ1])]})],"blendedInto":[makeQuery(id+"F2.opExtrude","SWEPT_FACE",FACE,{"disambiguationData":[OSD([subQ3,subQ2,subQ1])]})]}),makeQuery(id+"F13.opExtrude","SWEPT_EDGE",EDGE,{"disambiguationData":[OSD([sQuery(id+"F0.wireOp",EDGE,"E1.1"),sQuery(id+"F0.wireOp",EDGE,"E1.3"),sQuery(id+"F0.wireOp",EDGE,"E2"),sQuery(id+"F0.wireOp",EDGE,"E3"),sQuery(id+"F0.wireOp",EDGE,"E4"),sQuery(id+"F0.wireOp",EDGE,"E5"),sQuery(id+"F0.wireOp",EDGE,"E6"),sQuery(id+"F0.wireOp",EDGE,"E7"),sQuery(id+"F0.wireOp",EDGE,"E8.0"),sQuery(id+"F0.wireOp",EDGE,"E8.1"),sQuery(id+"F0.wireOp",EDGE,"E8.2"),sQuery(id+"F0.wireOp",EDGE,"E8.3"),sQuery(id+"F0.wireOp",EDGE,"E10.0"),sQuery(id+"F0.wireOp",EDGE,"E11.0"),sQuery(id+"F0.wireOp",EDGE,"E12.filletArc"),sQuery(id+"F0.wireOp",EDGE,"E13.filletArc"),sQuery(id+"F0.wireOp",EDGE,"E14.filletArc"),sQuery(id+"F0.wireOp",EDGE,"E15.filletArc"),sQuery(id+"F0.wireOp",EDGE,"E18.trimOffspring"),sQuery(id+"F0.wireOp",EDGE,"E19.trimOffspring"),sQuery(id+"F0.wireOp",EDGE,"E20.filletArc"),sQuery(id+"F0.wireOp",EDGE,"E21.filletArc"),sQuery(id+"F0.wireOp",EDGE,"E22.filletArc"),sQuery(id+"F0.wireOp",EDGE,"E23.filletArc"),sQuery(id+"F0.wireOp",EDGE,"E28.bottom"),sQuery(id+"F0.wireOp",EDGE,"E28.top"),sQuery(id+"F0.wireOp",EDGE,"E28.left"),sQuery(id+"F0.wireOp",EDGE,"E28.right"),sQuery(id+"F0.wireOp",EDGE,"E29.bottom"),sQuery(id+"F0.wireOp",EDGE,"E29.top"),sQuery(id+"F0.wireOp",EDGE,"E29.left"),sQuery(id+"F0.wireOp",EDGE,"E29.right"),sQuery(id+"F0.wireOp",EDGE,"E30.bottom"),sQuery(id+"F0.wireOp",EDGE,"E30.top"),sQuery(id+"F0.wireOp",EDGE,"E30.left"),sQuery(id+"F0.wireOp",EDGE,"E30.right"),sQuery(id+"F0.wireOp",EDGE,"E31.bottom"),sQuery(id+"F0.wireOp",EDGE,"E31.top"),sQuery(id+"F0.wireOp",EDGE,"E31.right"),sQuery(id+"F0.wireOp",EDGE,"E32.bottom"),sQuery(id+"F0.wireOp",EDGE,"E32.top"),subQ3,sQuery(id+"F0.wireOp",EDGE,"E33"),sQuery(id+"F0.wireOp",EDGE,"E34"),sQuery(id+"F0.wireOp",EDGE,"E35"),sQuery(id+"F0.wireOp",EDGE,"E36"),sQuery(id+"F0.wireOp",EDGE,"E41"),sQuery(id+"F0.wireOp",EDGE,"E42"),subQ2,sQuery(id+"F0.wireOp",EDGE,"E44"),subQ1,subQ0,sQuery(id+"F0.wireOp",EDGE,"E47"),sQuery(id+"F0.wireOp",EDGE,"E48"),sQuery(id+"F12.wireOp",EDGE,"E62")])]})]});}
            var Q5;
            Q5=makeQuery(id+"F13.opExtrude","SWEPT_EDGE",EDGE,{"disambiguationData":[OSD([sQuery(id+"F12.wireOp",EDGE,"E62"),sQuery(id+"F12.wireOp",EDGE,"E64")])]});
            var Q6;
            Q6=makeQuery(id+"F18.boolean.opBoolean","COPY",EDGE,{"derivedFrom":makeQuery(id+"F18.opExtrude","SWEPT_EDGE",EDGE,{"disambiguationData":[OSD([sQuery(id+"F0.wireOp",EDGE,"E1.3"),sQuery(id+"F0.wireOp",EDGE,"E31.top"),sQuery(id+"F0.wireOp",EDGE,"E32.top"),sQuery(id+"F0.wireOp",EDGE,"E35"),sQuery(id+"F0.wireOp",EDGE,"E36"),sQuery(id+"F0.wireOp",EDGE,"E41"),sQuery(id+"F0.wireOp",EDGE,"E46"),sQuery(id+"F9.wireOp",EDGE,"E55"),sQuery(id+"F12.wireOp",EDGE,"E69")])]})});
            var Q7;
            Q7=makeQuery(id+"F18.boolean.opBoolean","COPY",EDGE,{"derivedFrom":makeQuery(id+"F18.opExtrude","SWEPT_EDGE",EDGE,{"disambiguationData":[OSD([sQuery(id+"F9.wireOp",EDGE,"E54"),sQuery(id+"F12.wireOp",EDGE,"E69")])]})});
            fillet(context, id + "F19", {"entities" : qUnion([Q0, Q1, Q2, Q3, Q4, Q5, Q6, Q7]), "tangentPropagation" : true, "radius" : 5 * mm, "defaultsChanged" : false, "vertexSettings" : [], "allowEdgeOverflow" : false});
        }
    });
